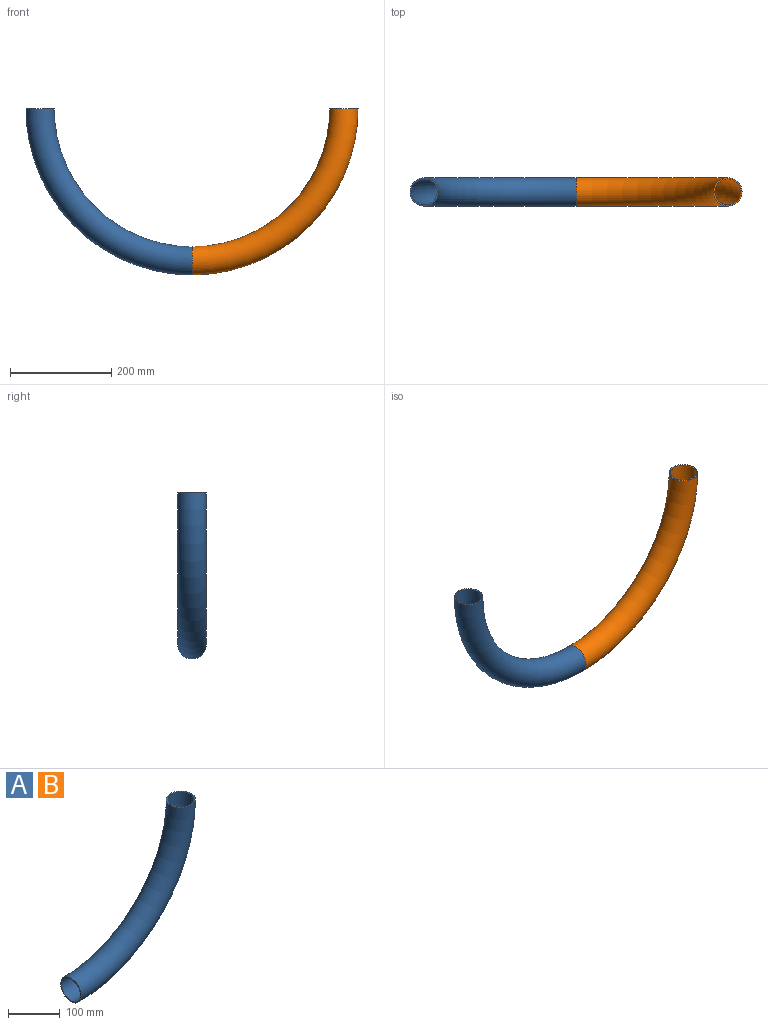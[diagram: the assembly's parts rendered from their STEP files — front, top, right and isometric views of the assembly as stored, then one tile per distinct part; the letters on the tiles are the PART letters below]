
ASSEMBLY  parts=2 mates=1
PART A: 4 faces, bbox 355x56x355 mm
  f0: torus R=300mm, axis (0,-1,0), area 75502.5mm2, adj f1,f2
  f1: plane 56x56mm, normal (-1,0,0), area 420.2mm2, adj f0,f3
  f2: plane 56x56mm, normal (0,0,1), area 420.2mm2, adj f0,f3
  f3: torus R=300mm, axis (0,-1,0), area 82904.7mm2, adj f1,f2
PART B: same geometry as A
PLACE A rot(axis=(0,0,1),180deg) t=(65.45,143.43,-119.56)mm
PLACE B t=(65.45,143.43,-119.56)mm
MATE fastened A.f1 <-> B.f1  axis (1,0,0) through (65.45,143.43,-119.56)mm
